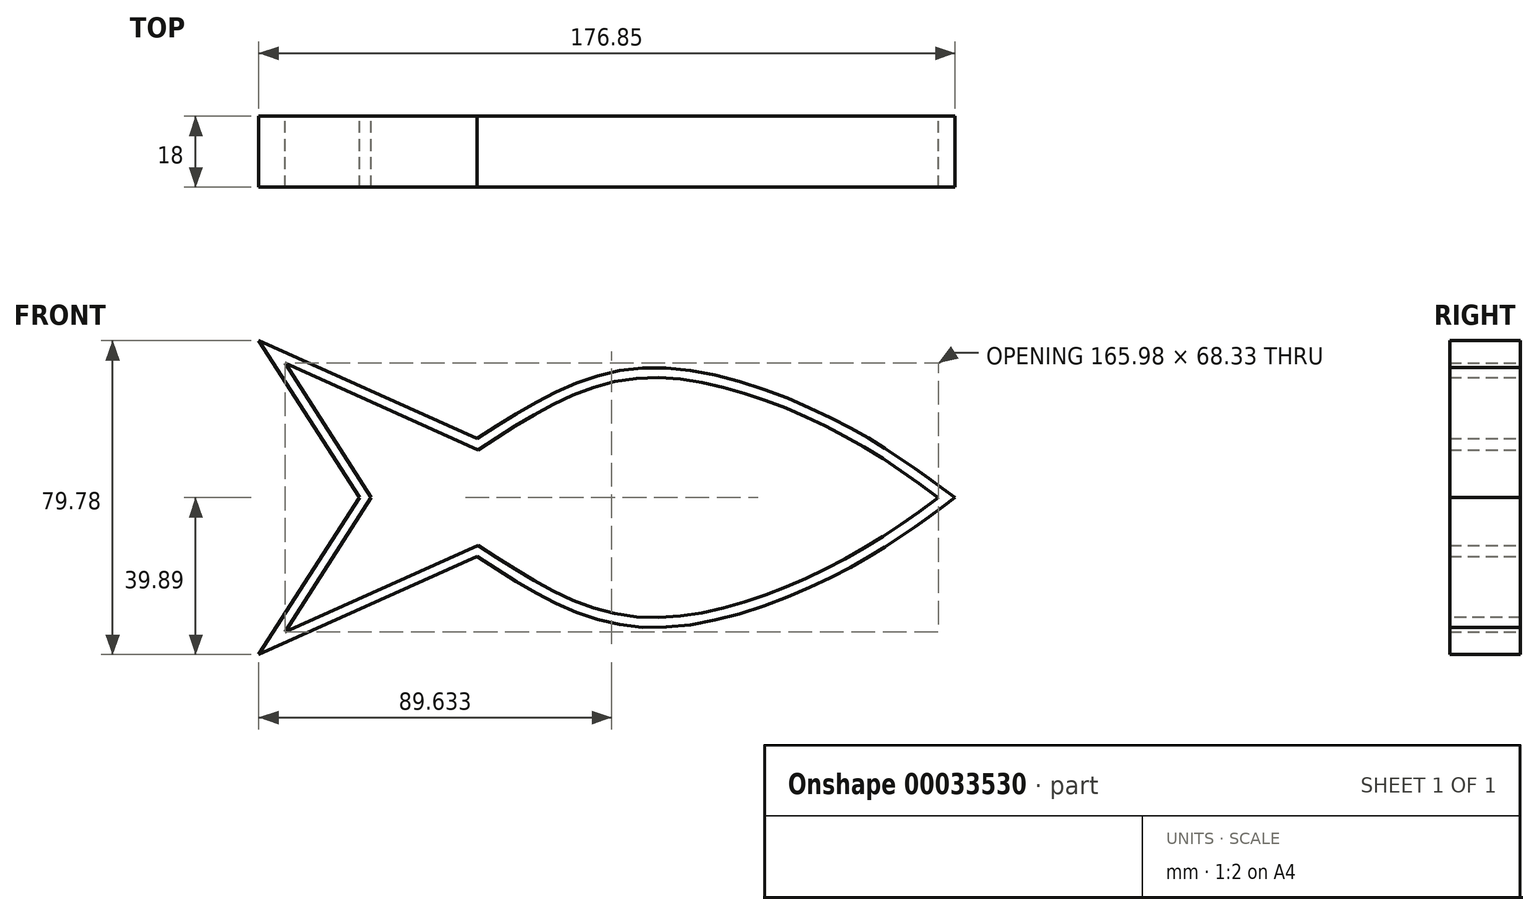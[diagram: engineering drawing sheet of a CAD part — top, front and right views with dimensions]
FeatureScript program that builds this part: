
annotation { "Feature Type Name" : "Feature", "Feature Type Description" : "" }
export const myFeature = defineFeature(function(context is Context, id is Id, definition is map)
    precondition{}
    {
        {
            var Q0;
            Q0=qCreatedBy(makeId("Front.planeOp"),FACE);
            var sketch = newSketch(context, id + "F0", { "sketchPlane" : qUnion([Q0])});
            skLineSegment(sketch, "E0", {"start": v(0, 0) * mm, "end": v(-24.35, 37.93) * mm});
            skLineSegment(sketch, "E1", {"start": v(-22.69, 38.58) * mm, "end": v(29.86, 14.98) * mm});
            skLineSegment(sketch, "E2", {"start": v(-22.69, 38.58) * mm, "end": v(-25.61, 39.9) * mm});
            skLineSegment(sketch, "E3", {"start": v(-24.35, 37.93) * mm, "end": v(-25.61, 39.9) * mm});
            skFitSpline(sketch, "E4", {"points": [v(29.86, 14.98) * mm, v(71.34, 32.9) * mm, v(121.94, 19.13) * mm, v(148.08, 2.31) * mm], "startDerivative": vector(113.12, 73.61) * mm, "endDerivative": vector(80.1, -58.62) * mm});
            skLineSegment(sketch, "E5", {"start": v(148.08, 2.31) * mm, "end": v(151.24, 0) * mm});
            skLineSegment(sketch, "E6.MirrorCS", {"start": v(0, 0) * mm, "end": v(-24.35, -37.93) * mm});
            skLineSegment(sketch, "E7.MirrorCS", {"start": v(-24.35, -37.93) * mm, "end": v(-25.61, -39.9) * mm});
            skLineSegment(sketch, "E8.MirrorCS", {"start": v(-22.69, -38.58) * mm, "end": v(-25.61, -39.9) * mm});
            skLineSegment(sketch, "E9.MirrorCS", {"start": v(-22.69, -38.58) * mm, "end": v(29.86, -14.98) * mm});
            skFitSpline(sketch, "E10.MirrorCS", {"points": [v(29.86, -14.98) * mm, v(71.34, -32.9) * mm, v(121.94, -19.13) * mm, v(148.08, -2.31) * mm], "startDerivative": vector(113.12, -73.61) * mm, "endDerivative": vector(80.1, 58.62) * mm});
            skLineSegment(sketch, "E11.MirrorCS", {"start": v(148.08, -2.31) * mm, "end": v(151.24, 0) * mm});
            skSolve(sketch);
        }
        {
            var Q0;
            Q0 = qSketchRegion(id + "F0", true);
            extrude(context, id + "F1", {"entities" : qUnion([Q0]), "depth" : 18 * mm});
        }
        {
            var Q0;
            Q0=makeQuery(id+"F1.opExtrude","CAP_FACE",FACE,{"disambiguationData":[OSD([sQuery(id+"F0.wireOp",EDGE,"E0"),sQuery(id+"F0.wireOp",EDGE,"E1"),sQuery(id+"F0.wireOp",EDGE,"E2"),sQuery(id+"F0.wireOp",EDGE,"E3"),sQuery(id+"F0.wireOp",EDGE,"E4"),sQuery(id+"F0.wireOp",EDGE,"E5"),sQuery(id+"F0.wireOp",EDGE,"E6.MirrorCS"),sQuery(id+"F0.wireOp",EDGE,"E7.MirrorCS"),sQuery(id+"F0.wireOp",EDGE,"E8.MirrorCS"),sQuery(id+"F0.wireOp",EDGE,"E9.MirrorCS"),sQuery(id+"F0.wireOp",EDGE,"E10.MirrorCS"),sQuery(id+"F0.wireOp",EDGE,"E11.MirrorCS")])],"isStart":false});
            var Q1;
            Q1=makeQuery(id+"F1.opExtrude","CAP_FACE",FACE,{"disambiguationData":[OSD([sQuery(id+"F0.wireOp",EDGE,"E0"),sQuery(id+"F0.wireOp",EDGE,"E1"),sQuery(id+"F0.wireOp",EDGE,"E2"),sQuery(id+"F0.wireOp",EDGE,"E3"),sQuery(id+"F0.wireOp",EDGE,"E4"),sQuery(id+"F0.wireOp",EDGE,"E5"),sQuery(id+"F0.wireOp",EDGE,"E6.MirrorCS"),sQuery(id+"F0.wireOp",EDGE,"E7.MirrorCS"),sQuery(id+"F0.wireOp",EDGE,"E8.MirrorCS"),sQuery(id+"F0.wireOp",EDGE,"E9.MirrorCS"),sQuery(id+"F0.wireOp",EDGE,"E10.MirrorCS"),sQuery(id+"F0.wireOp",EDGE,"E11.MirrorCS")])],"isStart":true});
            shell(context, id + "F2", {"entities" : qUnion([Q0, Q1]), "thickness" : 2.5 * mm});
        }
    });
